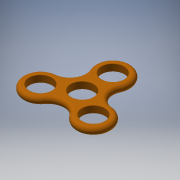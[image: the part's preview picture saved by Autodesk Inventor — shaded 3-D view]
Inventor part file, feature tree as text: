
AUTODESK INVENTOR PART (.ipt)
format: ipt  version: 2018 (Build 220112000, 112)  size: 209,408 bytes
history: native  units: mm
features: fillet x2, extrude x1, sketch x1
ambient origin geometry x8: Origin, YZ Plane, XZ Plane, XY Plane, X Axis, Y Axis, Z Axis, Center Point
bodies: Solid1 (feature_tree)
feature tree (4):
  extrude  "Extrusion1"  Depth=0.5mm
  fillet  "Fillet1"  Radius=30.0mm
  fillet  "Fillet2"  Radius=30.0mm
  sketch  "Sketch1"  dims[d0=22.0mm d1=22.0mm d2=30.0mm d3=30.0mm d5=360.0deg d7=6.0mm d8=6.0mm d9=6.0mm d10=15.0mm d11=15.0mm d12=15.0mm d13=7.0mm d14=0.0mm d15=0.5mm]
